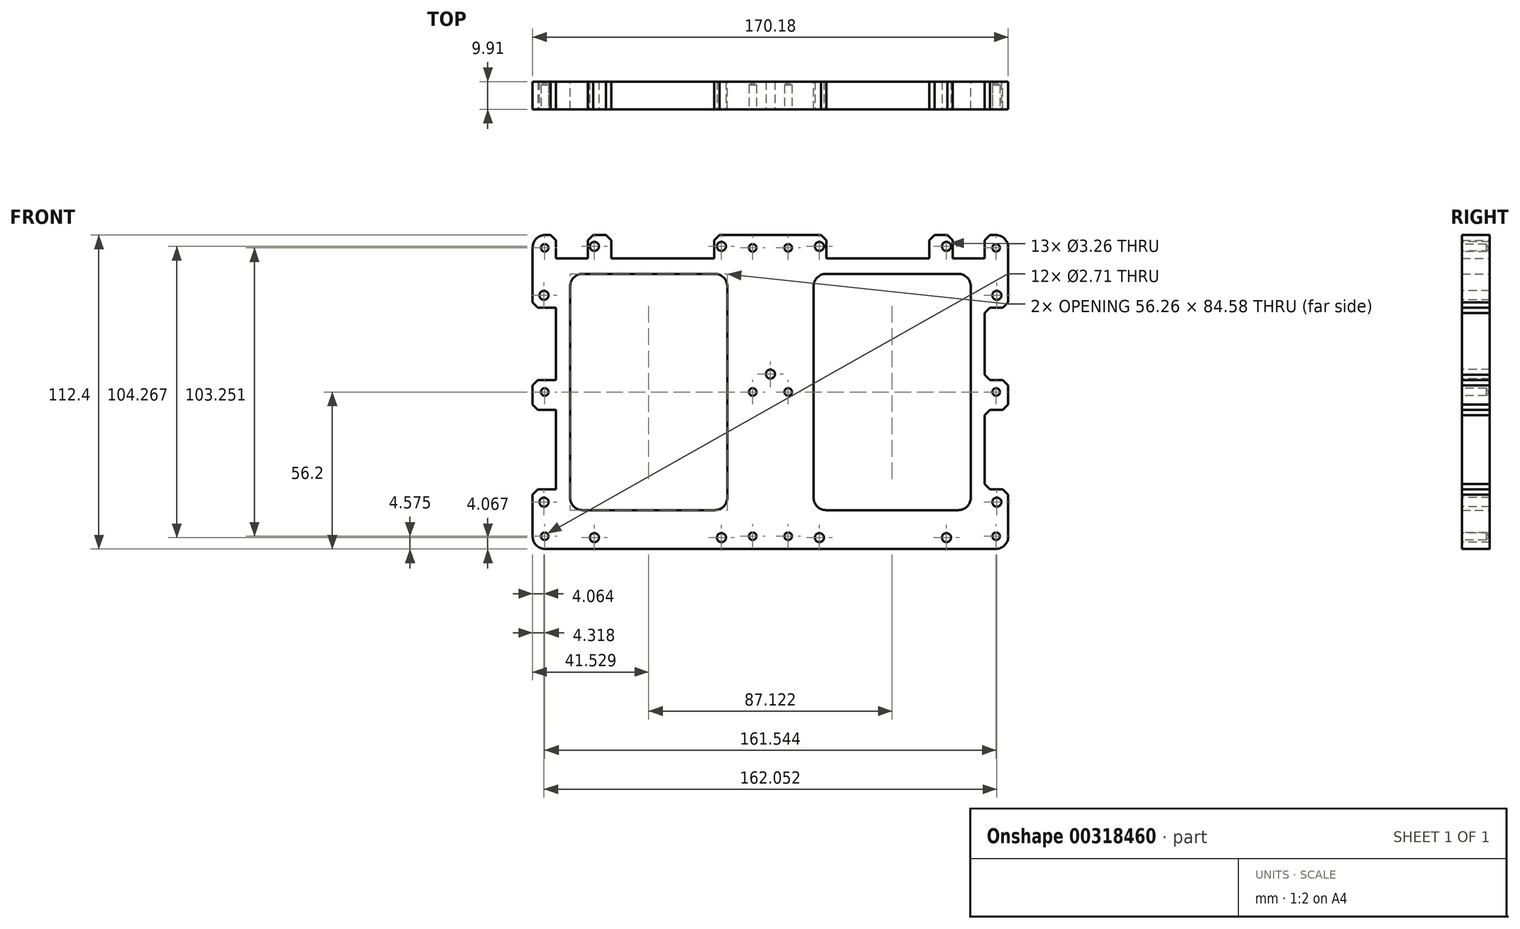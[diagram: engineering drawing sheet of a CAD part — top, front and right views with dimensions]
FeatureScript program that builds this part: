
annotation { "Feature Type Name" : "Feature", "Feature Type Description" : "" }
export const myFeature = defineFeature(function(context is Context, id is Id, definition is map)
    precondition{}
    {
        {
            var Q0;
            Q0=qCreatedBy(makeId("Front.planeOp"),FACE);
            var sketch = newSketch(context, id + "F0", { "sketchPlane" : qUnion([Q0])});
            skLineSegment(sketch, "E0.bottom", {"start": v(-80.64, -56.2) * mm, "end": v(80.64, -56.2) * mm});
            skLineSegment(sketch, "E0.top", {"start": v(-80.65, 56.2) * mm, "end": v(80.65, 56.2) * mm});
            skLineSegment(sketch, "E0.left", {"start": v(-85.09, -51.75) * mm, "end": v(-85.1, 51.75) * mm});
            skLineSegment(sketch, "E0.right", {"start": v(85.1, -56.2) * mm, "end": v(85.1, 56.2) * mm});
            skPoint(sketch, "E0.middle", {"position": v(0, 0) * mm});
            skLineSegment(sketch, "E1.bottom", {"start": v(-85.1, -34.86) * mm, "end": v(-76.7, -34.86) * mm});
            skLineSegment(sketch, "E1.top", {"start": v(-85.1, -6.41) * mm, "end": v(-76.7, -6.41) * mm});
            skLineSegment(sketch, "E1.left", {"start": v(-85.09, -34.86) * mm, "end": v(-85.09, -6.41) * mm});
            skLineSegment(sketch, "E1.right", {"start": v(-76.7, -34.86) * mm, "end": v(-76.7, -6.41) * mm});
            skLineSegment(sketch, "E2.bottom", {"start": v(-85.1, 4.25) * mm, "end": v(-76.7, 4.25) * mm});
            skLineSegment(sketch, "E2.top", {"start": v(-85.1, 30.16) * mm, "end": v(-76.7, 30.16) * mm});
            skLineSegment(sketch, "E2.left", {"start": v(-85.1, 4.25) * mm, "end": v(-85.1, 30.16) * mm});
            skLineSegment(sketch, "E2.right", {"start": v(-76.7, 4.25) * mm, "end": v(-76.7, 30.16) * mm});
            skLineSegment(sketch, "E3.bottom", {"start": v(-76.7, 56.2) * mm, "end": v(-65.28, 56.2) * mm});
            skLineSegment(sketch, "E3.top", {"start": v(-76.7, 47.82) * mm, "end": v(-65.28, 47.82) * mm});
            skLineSegment(sketch, "E3.left", {"start": v(-76.7, 56.2) * mm, "end": v(-76.7, 47.82) * mm});
            skLineSegment(sketch, "E3.right", {"start": v(-65.28, 56.2) * mm, "end": v(-65.28, 47.82) * mm});
            skPoint(sketch, "E4.oppositeSnap0", {"position": v(-71, 47.82) * mm});
            skLineSegment(sketch, "E4.bottom", {"start": v(-56.9, 56.2) * mm, "end": v(-20.07, 56.2) * mm});
            skLineSegment(sketch, "E4.top", {"start": v(-56.9, 47.82) * mm, "end": v(-20.07, 47.82) * mm});
            skLineSegment(sketch, "E4.left", {"start": v(-56.9, 56.2) * mm, "end": v(-56.9, 47.82) * mm});
            skLineSegment(sketch, "E4.right", {"start": v(-20.07, 56.2) * mm, "end": v(-20.07, 47.82) * mm});
            skLineSegment(sketch, "E5.bottom", {"start": v(-19.88, -42.3) * mm, "end": v(-67.25, -42.3) * mm});
            skLineSegment(sketch, "E5.top", {"start": v(-19.88, 42.3) * mm, "end": v(-67.25, 42.3) * mm});
            skLineSegment(sketch, "E5.left", {"start": v(-15.43, -37.85) * mm, "end": v(-15.43, 37.85) * mm});
            skLineSegment(sketch, "E5.right", {"start": v(-71.7, -37.85) * mm, "end": v(-71.7, 37.85) * mm});
            skPoint(sketch, "E5.middle", {"position": v(-43.56, 0) * mm});
            skPoint(sketch, "E6.visualSharp", {"position": v(-71.7, 42.3) * mm});
            skArc(sketch, "E6.filletArc", {"start": v(-67.25, 42.3) * mm, "mid": v(-70.39, 40.99) * mm, "end": v(-71.7, 37.85) * mm});
            skPoint(sketch, "E7.visualSharp", {"position": v(-15.43, 42.3) * mm});
            skArc(sketch, "E7.filletArc", {"start": v(-15.43, 37.85) * mm, "mid": v(-16.73, 40.99) * mm, "end": v(-19.88, 42.3) * mm});
            skPoint(sketch, "E8.visualSharp", {"position": v(-15.43, -42.3) * mm});
            skArc(sketch, "E8.filletArc", {"start": v(-19.88, -42.3) * mm, "mid": v(-16.73, -40.99) * mm, "end": v(-15.43, -37.85) * mm});
            skPoint(sketch, "E9.visualSharp", {"position": v(-71.7, -42.3) * mm});
            skArc(sketch, "E9.filletArc", {"start": v(-71.7, -37.85) * mm, "mid": v(-70.39, -40.99) * mm, "end": v(-67.25, -42.3) * mm});
            skArc(sketch, "E10.MirrorCS", {"start": v(71.7, -37.85) * mm, "mid": v(70.39, -40.99) * mm, "end": v(67.25, -42.3) * mm});
            skArc(sketch, "E11.MirrorCS", {"start": v(67.25, 42.3) * mm, "mid": v(70.39, 40.99) * mm, "end": v(71.7, 37.85) * mm});
            skLineSegment(sketch, "E12.MirrorCS", {"start": v(76.7, 47.82) * mm, "end": v(65.28, 47.82) * mm});
            skArc(sketch, "E13.MirrorCS", {"start": v(19.88, -42.3) * mm, "mid": v(16.73, -40.99) * mm, "end": v(15.43, -37.85) * mm});
            skArc(sketch, "E14.MirrorCS", {"start": v(15.43, 37.85) * mm, "mid": v(16.73, 40.99) * mm, "end": v(19.88, 42.3) * mm});
            skLineSegment(sketch, "E15.MirrorCS", {"start": v(65.28, 56.2) * mm, "end": v(65.28, 47.82) * mm});
            skLineSegment(sketch, "E16.MirrorCS", {"start": v(85.1, -6.41) * mm, "end": v(76.7, -6.41) * mm});
            skLineSegment(sketch, "E17.MirrorCS", {"start": v(56.9, 47.82) * mm, "end": v(20.07, 47.82) * mm});
            skPoint(sketch, "E18.MirrorP", {"position": v(71.7, 42.3) * mm});
            skLineSegment(sketch, "E19.MirrorCS", {"start": v(20.07, 56.2) * mm, "end": v(20.07, 47.82) * mm});
            skLineSegment(sketch, "E20.MirrorCS", {"start": v(56.9, 56.2) * mm, "end": v(20.07, 56.2) * mm});
            skLineSegment(sketch, "E21.MirrorCS", {"start": v(19.88, -42.3) * mm, "end": v(67.25, -42.3) * mm});
            skLineSegment(sketch, "E22.MirrorCS", {"start": v(71.7, -37.85) * mm, "end": v(71.7, 37.85) * mm});
            skPoint(sketch, "E23.MirrorP", {"position": v(71.7, -42.3) * mm});
            skLineSegment(sketch, "E24.MirrorCS", {"start": v(76.7, 56.2) * mm, "end": v(65.28, 56.2) * mm});
            skLineSegment(sketch, "E25.MirrorCS", {"start": v(76.7, 4.25) * mm, "end": v(76.7, 30.16) * mm});
            skLineSegment(sketch, "E26.MirrorCS", {"start": v(85.1, 4.25) * mm, "end": v(85.1, 30.16) * mm});
            skLineSegment(sketch, "E27.MirrorCS", {"start": v(85.1, 30.16) * mm, "end": v(76.7, 30.16) * mm});
            skLineSegment(sketch, "E28.MirrorCS", {"start": v(85.1, 4.25) * mm, "end": v(76.7, 4.25) * mm});
            skLineSegment(sketch, "E29.MirrorCS", {"start": v(76.7, -34.86) * mm, "end": v(76.7, -6.41) * mm});
            skLineSegment(sketch, "E30.MirrorCS", {"start": v(85.09, -34.86) * mm, "end": v(85.09, -6.41) * mm});
            skPoint(sketch, "E31.MirrorP", {"position": v(15.43, -42.3) * mm});
            skLineSegment(sketch, "E32.MirrorCS", {"start": v(85.1, -34.86) * mm, "end": v(76.7, -34.86) * mm});
            skLineSegment(sketch, "E33.MirrorCS", {"start": v(85.09, -51.75) * mm, "end": v(85.1, 51.75) * mm});
            skLineSegment(sketch, "E34.MirrorCS", {"start": v(76.7, 56.2) * mm, "end": v(76.7, 47.82) * mm});
            skLineSegment(sketch, "E35.MirrorCS", {"start": v(19.88, 42.3) * mm, "end": v(67.25, 42.3) * mm});
            skLineSegment(sketch, "E36.MirrorCS", {"start": v(15.43, -37.85) * mm, "end": v(15.43, 37.85) * mm});
            skPoint(sketch, "E37.MirrorP", {"position": v(71, 47.82) * mm});
            skLineSegment(sketch, "E38.MirrorCS", {"start": v(56.9, 56.2) * mm, "end": v(56.9, 47.82) * mm});
            skPoint(sketch, "E39.MirrorP", {"position": v(15.43, 42.3) * mm});
            skPoint(sketch, "E40.MirrorP", {"position": v(43.56, 0) * mm});
            skPoint(sketch, "E41.visualSharp", {"position": v(-85.1, 56.2) * mm});
            skArc(sketch, "E41.filletArc", {"start": v(-80.65, 56.2) * mm, "mid": v(-83.79, 54.9) * mm, "end": v(-85.1, 51.75) * mm});
            skPoint(sketch, "E42.visualSharp", {"position": v(-85.09, -56.2) * mm});
            skArc(sketch, "E42.filletArc", {"start": v(-85.09, -51.75) * mm, "mid": v(-83.79, -54.9) * mm, "end": v(-80.64, -56.2) * mm});
            skPoint(sketch, "E43.visualSharp", {"position": v(85.1, -56.2) * mm});
            skArc(sketch, "E43.filletArc", {"start": v(80.64, -56.2) * mm, "mid": v(83.79, -54.9) * mm, "end": v(85.09, -51.75) * mm});
            skPoint(sketch, "E44.visualSharp", {"position": v(85.09, 56.2) * mm});
            skArc(sketch, "E44.filletArc", {"start": v(85.1, 51.75) * mm, "mid": v(83.79, 54.9) * mm, "end": v(80.65, 56.2) * mm});
            skSolve(sketch);
        }
        {
            var Q0;
            {var subQ12=sQuery(id+"F0.wireOp",EDGE,"E0.bottom");Q0=makeQuery(id+"F0.imprint","IMPRINT",FACE,{"disambiguationData":[TD([[makeQuery(id+"F0.imprint","IMPRINT",EDGE,{"derivedFrom":subQ12}),1.0]])]});}
            extrude(context, id + "F1", {"entities" : qUnion([Q0]), "depth" : 9.9 * mm});
        }
        {
            var Q0;
            Q0=makeQuery(id+"F1.opExtrude","SWEPT_EDGE",EDGE,{"disambiguationData":[OSD([sQuery(id+"F0.wireOp",EDGE,"E0.left"),sQuery(id+"F0.wireOp",EDGE,"E1.bottom"),sQuery(id+"F0.wireOp",EDGE,"E1.left")])]});
            var Q1;
            Q1=makeQuery(id+"F1.opExtrude","SWEPT_EDGE",EDGE,{"disambiguationData":[OSD([sQuery(id+"F0.wireOp",EDGE,"E0.left"),sQuery(id+"F0.wireOp",EDGE,"E1.top"),sQuery(id+"F0.wireOp",EDGE,"E1.left")])]});
            var Q2;
            Q2=makeQuery(id+"F1.opExtrude","SWEPT_EDGE",EDGE,{"disambiguationData":[OSD([sQuery(id+"F0.wireOp",EDGE,"E0.left"),sQuery(id+"F0.wireOp",EDGE,"E2.bottom"),sQuery(id+"F0.wireOp",EDGE,"E2.left")])]});
            var Q3;
            Q3=makeQuery(id+"F1.opExtrude","SWEPT_EDGE",EDGE,{"disambiguationData":[OSD([sQuery(id+"F0.wireOp",EDGE,"E0.left"),sQuery(id+"F0.wireOp",EDGE,"E2.top"),sQuery(id+"F0.wireOp",EDGE,"E2.left")])]});
            var Q4;
            Q4=makeQuery(id+"F1.opExtrude","SWEPT_EDGE",EDGE,{"disambiguationData":[OSD([sQuery(id+"F0.wireOp",EDGE,"E0.top"),sQuery(id+"F0.wireOp",EDGE,"E3.bottom"),sQuery(id+"F0.wireOp",EDGE,"E3.left")])]});
            var Q5;
            Q5=makeQuery(id+"F1.opExtrude","SWEPT_EDGE",EDGE,{"disambiguationData":[OSD([sQuery(id+"F0.wireOp",EDGE,"E0.top"),sQuery(id+"F0.wireOp",EDGE,"E3.bottom"),sQuery(id+"F0.wireOp",EDGE,"E3.right")])]});
            var Q6;
            Q6=makeQuery(id+"F1.opExtrude","SWEPT_EDGE",EDGE,{"disambiguationData":[OSD([sQuery(id+"F0.wireOp",EDGE,"E0.top"),sQuery(id+"F0.wireOp",EDGE,"E4.bottom"),sQuery(id+"F0.wireOp",EDGE,"E4.left")])]});
            var Q7;
            Q7=makeQuery(id+"F1.opExtrude","SWEPT_EDGE",EDGE,{"disambiguationData":[OSD([sQuery(id+"F0.wireOp",EDGE,"E0.top"),sQuery(id+"F0.wireOp",EDGE,"E4.bottom"),sQuery(id+"F0.wireOp",EDGE,"E4.right")])]});
            var Q8;
            Q8=makeQuery(id+"F1.opExtrude","SWEPT_EDGE",EDGE,{"disambiguationData":[OSD([sQuery(id+"F0.wireOp",EDGE,"E0.top"),sQuery(id+"F0.wireOp",EDGE,"E19.MirrorCS"),sQuery(id+"F0.wireOp",EDGE,"E20.MirrorCS")])]});
            var Q9;
            Q9=makeQuery(id+"F1.opExtrude","SWEPT_EDGE",EDGE,{"disambiguationData":[OSD([sQuery(id+"F0.wireOp",EDGE,"E0.top"),sQuery(id+"F0.wireOp",EDGE,"E15.MirrorCS"),sQuery(id+"F0.wireOp",EDGE,"E24.MirrorCS")])]});
            var Q10;
            Q10=makeQuery(id+"F1.opExtrude","SWEPT_EDGE",EDGE,{"disambiguationData":[OSD([sQuery(id+"F0.wireOp",EDGE,"E0.top"),sQuery(id+"F0.wireOp",EDGE,"E20.MirrorCS"),sQuery(id+"F0.wireOp",EDGE,"E38.MirrorCS")])]});
            var Q11;
            Q11=makeQuery(id+"F1.opExtrude","SWEPT_EDGE",EDGE,{"disambiguationData":[OSD([sQuery(id+"F0.wireOp",EDGE,"E0.top"),sQuery(id+"F0.wireOp",EDGE,"E24.MirrorCS"),sQuery(id+"F0.wireOp",EDGE,"E34.MirrorCS")])]});
            var Q12;
            Q12=makeQuery(id+"F1.opExtrude","SWEPT_EDGE",EDGE,{"disambiguationData":[OSD([sQuery(id+"F0.wireOp",EDGE,"E27.MirrorCS"),sQuery(id+"F0.wireOp",EDGE,"E33.MirrorCS")])]});
            var Q13;
            Q13=makeQuery(id+"F1.opExtrude","SWEPT_EDGE",EDGE,{"disambiguationData":[OSD([sQuery(id+"F0.wireOp",EDGE,"E28.MirrorCS"),sQuery(id+"F0.wireOp",EDGE,"E33.MirrorCS")])]});
            var Q14;
            Q14=makeQuery(id+"F1.opExtrude","SWEPT_EDGE",EDGE,{"disambiguationData":[OSD([sQuery(id+"F0.wireOp",EDGE,"E16.MirrorCS"),sQuery(id+"F0.wireOp",EDGE,"E33.MirrorCS")])]});
            var Q15;
            Q15=makeQuery(id+"F1.opExtrude","SWEPT_EDGE",EDGE,{"disambiguationData":[OSD([sQuery(id+"F0.wireOp",EDGE,"E32.MirrorCS"),sQuery(id+"F0.wireOp",EDGE,"E33.MirrorCS")])]});
            chamfer(context, id + "F2", {"entities" : qUnion([Q0, Q1, Q2, Q3, Q4, Q5, Q6, Q7, Q8, Q9, Q10, Q11, Q12, Q13, Q14, Q15]), "width" : 1.9 * mm, "tangentPropagation" : true});
        }
        {
            var Q0;
            Q0=makeQuery(id+"F1.opExtrude","CAP_FACE",FACE,{"disambiguationData":[OSD([sQuery(id+"F0.wireOp",EDGE,"E0.bottom"),sQuery(id+"F0.wireOp",EDGE,"E0.top"),sQuery(id+"F0.wireOp",EDGE,"E0.left"),sQuery(id+"F0.wireOp",EDGE,"E1.bottom"),sQuery(id+"F0.wireOp",EDGE,"E1.top"),sQuery(id+"F0.wireOp",EDGE,"E1.right"),sQuery(id+"F0.wireOp",EDGE,"E2.bottom"),sQuery(id+"F0.wireOp",EDGE,"E2.top"),sQuery(id+"F0.wireOp",EDGE,"E2.right"),sQuery(id+"F0.wireOp",EDGE,"E3.top"),sQuery(id+"F0.wireOp",EDGE,"E3.left"),sQuery(id+"F0.wireOp",EDGE,"E3.right"),sQuery(id+"F0.wireOp",EDGE,"E4.top"),sQuery(id+"F0.wireOp",EDGE,"E4.left"),sQuery(id+"F0.wireOp",EDGE,"E4.right"),sQuery(id+"F0.wireOp",EDGE,"E5.bottom"),sQuery(id+"F0.wireOp",EDGE,"E5.top"),sQuery(id+"F0.wireOp",EDGE,"E5.left"),sQuery(id+"F0.wireOp",EDGE,"E5.right"),sQuery(id+"F0.wireOp",EDGE,"E6.filletArc"),sQuery(id+"F0.wireOp",EDGE,"E7.filletArc"),sQuery(id+"F0.wireOp",EDGE,"E8.filletArc"),sQuery(id+"F0.wireOp",EDGE,"E9.filletArc"),sQuery(id+"F0.wireOp",EDGE,"E10.MirrorCS"),sQuery(id+"F0.wireOp",EDGE,"E11.MirrorCS"),sQuery(id+"F0.wireOp",EDGE,"E12.MirrorCS"),sQuery(id+"F0.wireOp",EDGE,"E13.MirrorCS"),sQuery(id+"F0.wireOp",EDGE,"E14.MirrorCS"),sQuery(id+"F0.wireOp",EDGE,"E15.MirrorCS"),sQuery(id+"F0.wireOp",EDGE,"E16.MirrorCS"),sQuery(id+"F0.wireOp",EDGE,"E17.MirrorCS"),sQuery(id+"F0.wireOp",EDGE,"E19.MirrorCS"),sQuery(id+"F0.wireOp",EDGE,"E21.MirrorCS"),sQuery(id+"F0.wireOp",EDGE,"E22.MirrorCS"),sQuery(id+"F0.wireOp",EDGE,"E25.MirrorCS"),sQuery(id+"F0.wireOp",EDGE,"E27.MirrorCS"),sQuery(id+"F0.wireOp",EDGE,"E28.MirrorCS"),sQuery(id+"F0.wireOp",EDGE,"E29.MirrorCS"),sQuery(id+"F0.wireOp",EDGE,"E32.MirrorCS"),sQuery(id+"F0.wireOp",EDGE,"E33.MirrorCS"),sQuery(id+"F0.wireOp",EDGE,"E34.MirrorCS"),sQuery(id+"F0.wireOp",EDGE,"E35.MirrorCS"),sQuery(id+"F0.wireOp",EDGE,"E36.MirrorCS"),sQuery(id+"F0.wireOp",EDGE,"E38.MirrorCS"),sQuery(id+"F0.wireOp",EDGE,"E41.filletArc"),sQuery(id+"F0.wireOp",EDGE,"E42.filletArc"),sQuery(id+"F0.wireOp",EDGE,"E43.filletArc"),sQuery(id+"F0.wireOp",EDGE,"E44.filletArc")])],"isStart":false});
            var sketch = newSketch(context, id + "F3", { "sketchPlane" : qUnion([Q0])});
            skPoint(sketch, "E45", {"position": v(-80.77, 51.63) * mm});
            skPoint(sketch, "E46", {"position": v(-80.77, 0) * mm});
            skPoint(sketch, "E47", {"position": v(-80.77, -51.63) * mm});
            skPoint(sketch, "E48", {"position": v(-6.35, -51.63) * mm});
            skPoint(sketch, "E49", {"position": v(-6.35, 0) * mm});
            skPoint(sketch, "E50", {"position": v(-6.35, 51.63) * mm});
            skPoint(sketch, "E51.MirrorP", {"position": v(80.77, -51.63) * mm});
            skPoint(sketch, "E52.MirrorP", {"position": v(80.77, 51.63) * mm});
            skPoint(sketch, "E53.MirrorP", {"position": v(6.35, 51.63) * mm});
            skPoint(sketch, "E54.MirrorP", {"position": v(6.35, -51.63) * mm});
            skPoint(sketch, "E55.MirrorP", {"position": v(6.35, 0) * mm});
            skPoint(sketch, "E56.MirrorP", {"position": v(80.77, 0) * mm});
            skSolve(sketch);
        }
        {
            var Q0;
            Q0=sQuery(id+"F3.wireOp",VERTEX,"E45");
            var Q1;
            Q1=sQuery(id+"F3.wireOp",VERTEX,"E46");
            var Q2;
            Q2=sQuery(id+"F3.wireOp",VERTEX,"E47");
            var Q3;
            Q3=sQuery(id+"F3.wireOp",VERTEX,"E48");
            var Q4;
            Q4=sQuery(id+"F3.wireOp",VERTEX,"E49");
            var Q5;
            Q5=sQuery(id+"F3.wireOp",VERTEX,"E50");
            var Q6;
            Q6=sQuery(id+"F3.wireOp",VERTEX,"E53.MirrorP");
            var Q7;
            Q7=sQuery(id+"F3.wireOp",VERTEX,"E55.MirrorP");
            var Q8;
            Q8=sQuery(id+"F3.wireOp",VERTEX,"E54.MirrorP");
            var Q9;
            Q9=sQuery(id+"F3.wireOp",VERTEX,"E51.MirrorP");
            var Q10;
            Q10=sQuery(id+"F3.wireOp",VERTEX,"E56.MirrorP");
            var Q11;
            Q11=sQuery(id+"F3.wireOp",VERTEX,"E52.MirrorP");
            var Q12;
            Q12=makeQuery(id+"F1.opExtrude","SWEPT_BODY",BODY,{"disambiguationData":[OSD([sQuery(id+"F0.wireOp",EDGE,"E0.bottom"),sQuery(id+"F0.wireOp",EDGE,"E0.top"),sQuery(id+"F0.wireOp",EDGE,"E0.left"),sQuery(id+"F0.wireOp",EDGE,"E1.bottom"),sQuery(id+"F0.wireOp",EDGE,"E1.top"),sQuery(id+"F0.wireOp",EDGE,"E1.right"),sQuery(id+"F0.wireOp",EDGE,"E2.bottom"),sQuery(id+"F0.wireOp",EDGE,"E2.top"),sQuery(id+"F0.wireOp",EDGE,"E2.right"),sQuery(id+"F0.wireOp",EDGE,"E3.top"),sQuery(id+"F0.wireOp",EDGE,"E3.left"),sQuery(id+"F0.wireOp",EDGE,"E3.right"),sQuery(id+"F0.wireOp",EDGE,"E4.top"),sQuery(id+"F0.wireOp",EDGE,"E4.left"),sQuery(id+"F0.wireOp",EDGE,"E4.right"),sQuery(id+"F0.wireOp",EDGE,"E5.bottom"),sQuery(id+"F0.wireOp",EDGE,"E5.top"),sQuery(id+"F0.wireOp",EDGE,"E5.left"),sQuery(id+"F0.wireOp",EDGE,"E5.right"),sQuery(id+"F0.wireOp",EDGE,"E6.filletArc"),sQuery(id+"F0.wireOp",EDGE,"E7.filletArc"),sQuery(id+"F0.wireOp",EDGE,"E8.filletArc"),sQuery(id+"F0.wireOp",EDGE,"E9.filletArc"),sQuery(id+"F0.wireOp",EDGE,"E10.MirrorCS"),sQuery(id+"F0.wireOp",EDGE,"E11.MirrorCS"),sQuery(id+"F0.wireOp",EDGE,"E12.MirrorCS"),sQuery(id+"F0.wireOp",EDGE,"E13.MirrorCS"),sQuery(id+"F0.wireOp",EDGE,"E14.MirrorCS"),sQuery(id+"F0.wireOp",EDGE,"E15.MirrorCS"),sQuery(id+"F0.wireOp",EDGE,"E16.MirrorCS"),sQuery(id+"F0.wireOp",EDGE,"E17.MirrorCS"),sQuery(id+"F0.wireOp",EDGE,"E19.MirrorCS"),sQuery(id+"F0.wireOp",EDGE,"E21.MirrorCS"),sQuery(id+"F0.wireOp",EDGE,"E22.MirrorCS"),sQuery(id+"F0.wireOp",EDGE,"E25.MirrorCS"),sQuery(id+"F0.wireOp",EDGE,"E27.MirrorCS"),sQuery(id+"F0.wireOp",EDGE,"E28.MirrorCS"),sQuery(id+"F0.wireOp",EDGE,"E29.MirrorCS"),sQuery(id+"F0.wireOp",EDGE,"E32.MirrorCS"),sQuery(id+"F0.wireOp",EDGE,"E33.MirrorCS"),sQuery(id+"F0.wireOp",EDGE,"E34.MirrorCS"),sQuery(id+"F0.wireOp",EDGE,"E35.MirrorCS"),sQuery(id+"F0.wireOp",EDGE,"E36.MirrorCS"),sQuery(id+"F0.wireOp",EDGE,"E38.MirrorCS"),sQuery(id+"F0.wireOp",EDGE,"E41.filletArc"),sQuery(id+"F0.wireOp",EDGE,"E42.filletArc"),sQuery(id+"F0.wireOp",EDGE,"E43.filletArc"),sQuery(id+"F0.wireOp",EDGE,"E44.filletArc")])]});
            hole(context, id + "F4", {"style" : HoleStyle.SIMPLE, "endStyle" : HoleEndStyle.BLIND, "standardTappedOrClearance" : lookupTablePath({ "standard" : "ANSI", "engagement" : "75%", "pitch" : "32 tpi", "size" : "#6", "type" : "Tapped" }), "standardBlindInLast" : lookupTablePath({ "standard" : "ANSI", "engagement" : "75%", "pitch" : "32 tpi", "size" : "#6", "type" : "Tapped" }), "holeDiameter" : 2.7 * mm, "showTappedDepth" : true, "holeDepth" : 8.73 * mm, "tappedDepth" : 6.35 * mm, "tapClearance" : 3, "locations" : qUnion([Q0, Q1, Q2, Q3, Q4, Q5, Q6, Q7, Q8, Q9, Q10, Q11]), "scope" : qUnion([Q12]), "majorDiameter" : 3.5 * mm});
        }
        {
            var Q0;
            Q0=makeQuery(id+"F1.opExtrude","CAP_FACE",FACE,{"disambiguationData":[OSD([sQuery(id+"F0.wireOp",EDGE,"E0.bottom"),sQuery(id+"F0.wireOp",EDGE,"E0.top"),sQuery(id+"F0.wireOp",EDGE,"E0.left"),sQuery(id+"F0.wireOp",EDGE,"E1.bottom"),sQuery(id+"F0.wireOp",EDGE,"E1.top"),sQuery(id+"F0.wireOp",EDGE,"E1.right"),sQuery(id+"F0.wireOp",EDGE,"E2.bottom"),sQuery(id+"F0.wireOp",EDGE,"E2.top"),sQuery(id+"F0.wireOp",EDGE,"E2.right"),sQuery(id+"F0.wireOp",EDGE,"E3.top"),sQuery(id+"F0.wireOp",EDGE,"E3.left"),sQuery(id+"F0.wireOp",EDGE,"E3.right"),sQuery(id+"F0.wireOp",EDGE,"E4.top"),sQuery(id+"F0.wireOp",EDGE,"E4.left"),sQuery(id+"F0.wireOp",EDGE,"E4.right"),sQuery(id+"F0.wireOp",EDGE,"E5.bottom"),sQuery(id+"F0.wireOp",EDGE,"E5.top"),sQuery(id+"F0.wireOp",EDGE,"E5.left"),sQuery(id+"F0.wireOp",EDGE,"E5.right"),sQuery(id+"F0.wireOp",EDGE,"E6.filletArc"),sQuery(id+"F0.wireOp",EDGE,"E7.filletArc"),sQuery(id+"F0.wireOp",EDGE,"E8.filletArc"),sQuery(id+"F0.wireOp",EDGE,"E9.filletArc"),sQuery(id+"F0.wireOp",EDGE,"E10.MirrorCS"),sQuery(id+"F0.wireOp",EDGE,"E11.MirrorCS"),sQuery(id+"F0.wireOp",EDGE,"E12.MirrorCS"),sQuery(id+"F0.wireOp",EDGE,"E13.MirrorCS"),sQuery(id+"F0.wireOp",EDGE,"E14.MirrorCS"),sQuery(id+"F0.wireOp",EDGE,"E15.MirrorCS"),sQuery(id+"F0.wireOp",EDGE,"E16.MirrorCS"),sQuery(id+"F0.wireOp",EDGE,"E17.MirrorCS"),sQuery(id+"F0.wireOp",EDGE,"E19.MirrorCS"),sQuery(id+"F0.wireOp",EDGE,"E21.MirrorCS"),sQuery(id+"F0.wireOp",EDGE,"E22.MirrorCS"),sQuery(id+"F0.wireOp",EDGE,"E25.MirrorCS"),sQuery(id+"F0.wireOp",EDGE,"E27.MirrorCS"),sQuery(id+"F0.wireOp",EDGE,"E28.MirrorCS"),sQuery(id+"F0.wireOp",EDGE,"E29.MirrorCS"),sQuery(id+"F0.wireOp",EDGE,"E32.MirrorCS"),sQuery(id+"F0.wireOp",EDGE,"E33.MirrorCS"),sQuery(id+"F0.wireOp",EDGE,"E34.MirrorCS"),sQuery(id+"F0.wireOp",EDGE,"E35.MirrorCS"),sQuery(id+"F0.wireOp",EDGE,"E36.MirrorCS"),sQuery(id+"F0.wireOp",EDGE,"E38.MirrorCS"),sQuery(id+"F0.wireOp",EDGE,"E41.filletArc"),sQuery(id+"F0.wireOp",EDGE,"E42.filletArc"),sQuery(id+"F0.wireOp",EDGE,"E43.filletArc"),sQuery(id+"F0.wireOp",EDGE,"E44.filletArc")])],"isStart":false});
            var sketch = newSketch(context, id + "F5", { "sketchPlane" : qUnion([Q0])});
            skPoint(sketch, "E57", {"position": v(0, 6.41) * mm});
            skPoint(sketch, "E58", {"position": v(-17.53, 52.13) * mm});
            skPoint(sketch, "E59", {"position": v(-63, 52.13) * mm});
            skPoint(sketch, "E60", {"position": v(-81.03, 34.6) * mm});
            skPoint(sketch, "E61", {"position": v(-81.03, -39.43) * mm});
            skPoint(sketch, "E62", {"position": v(-63, -52.13) * mm});
            skPoint(sketch, "E63", {"position": v(-17.53, -52.13) * mm});
            skPoint(sketch, "E64.MirrorP", {"position": v(17.53, 52.13) * mm});
            skPoint(sketch, "E65.MirrorP", {"position": v(81.03, -39.43) * mm});
            skPoint(sketch, "E66.MirrorP", {"position": v(81.03, 34.6) * mm});
            skPoint(sketch, "E67.MirrorP", {"position": v(17.53, -52.13) * mm});
            skPoint(sketch, "E68.MirrorP", {"position": v(63, -52.13) * mm});
            skPoint(sketch, "E69.MirrorP", {"position": v(63, 52.13) * mm});
            skSolve(sketch);
        }
        {
            var Q0;
            Q0=sQuery(id+"F5.wireOp",VERTEX,"E60");
            var Q1;
            Q1=sQuery(id+"F5.wireOp",VERTEX,"E59");
            var Q2;
            Q2=sQuery(id+"F5.wireOp",VERTEX,"E61");
            var Q3;
            Q3=sQuery(id+"F5.wireOp",VERTEX,"E62");
            var Q4;
            Q4=sQuery(id+"F5.wireOp",VERTEX,"E58");
            var Q5;
            Q5=sQuery(id+"F5.wireOp",VERTEX,"E63");
            var Q6;
            Q6=sQuery(id+"F5.wireOp",VERTEX,"E57");
            var Q7;
            Q7=sQuery(id+"F5.wireOp",VERTEX,"E67.MirrorP");
            var Q8;
            Q8=sQuery(id+"F5.wireOp",VERTEX,"E68.MirrorP");
            var Q9;
            Q9=sQuery(id+"F5.wireOp",VERTEX,"E65.MirrorP");
            var Q10;
            Q10=sQuery(id+"F5.wireOp",VERTEX,"E66.MirrorP");
            var Q11;
            Q11=sQuery(id+"F5.wireOp",VERTEX,"E69.MirrorP");
            var Q12;
            Q12=sQuery(id+"F5.wireOp",VERTEX,"E64.MirrorP");
            var Q13;
            Q13=makeQuery(id+"F1.opExtrude","SWEPT_BODY",BODY,{"disambiguationData":[OSD([sQuery(id+"F0.wireOp",EDGE,"E0.bottom"),sQuery(id+"F0.wireOp",EDGE,"E0.top"),sQuery(id+"F0.wireOp",EDGE,"E0.left"),sQuery(id+"F0.wireOp",EDGE,"E1.bottom"),sQuery(id+"F0.wireOp",EDGE,"E1.top"),sQuery(id+"F0.wireOp",EDGE,"E1.right"),sQuery(id+"F0.wireOp",EDGE,"E2.bottom"),sQuery(id+"F0.wireOp",EDGE,"E2.top"),sQuery(id+"F0.wireOp",EDGE,"E2.right"),sQuery(id+"F0.wireOp",EDGE,"E3.top"),sQuery(id+"F0.wireOp",EDGE,"E3.left"),sQuery(id+"F0.wireOp",EDGE,"E3.right"),sQuery(id+"F0.wireOp",EDGE,"E4.top"),sQuery(id+"F0.wireOp",EDGE,"E4.left"),sQuery(id+"F0.wireOp",EDGE,"E4.right"),sQuery(id+"F0.wireOp",EDGE,"E5.bottom"),sQuery(id+"F0.wireOp",EDGE,"E5.top"),sQuery(id+"F0.wireOp",EDGE,"E5.left"),sQuery(id+"F0.wireOp",EDGE,"E5.right"),sQuery(id+"F0.wireOp",EDGE,"E6.filletArc"),sQuery(id+"F0.wireOp",EDGE,"E7.filletArc"),sQuery(id+"F0.wireOp",EDGE,"E8.filletArc"),sQuery(id+"F0.wireOp",EDGE,"E9.filletArc"),sQuery(id+"F0.wireOp",EDGE,"E10.MirrorCS"),sQuery(id+"F0.wireOp",EDGE,"E11.MirrorCS"),sQuery(id+"F0.wireOp",EDGE,"E12.MirrorCS"),sQuery(id+"F0.wireOp",EDGE,"E13.MirrorCS"),sQuery(id+"F0.wireOp",EDGE,"E14.MirrorCS"),sQuery(id+"F0.wireOp",EDGE,"E15.MirrorCS"),sQuery(id+"F0.wireOp",EDGE,"E16.MirrorCS"),sQuery(id+"F0.wireOp",EDGE,"E17.MirrorCS"),sQuery(id+"F0.wireOp",EDGE,"E19.MirrorCS"),sQuery(id+"F0.wireOp",EDGE,"E21.MirrorCS"),sQuery(id+"F0.wireOp",EDGE,"E22.MirrorCS"),sQuery(id+"F0.wireOp",EDGE,"E25.MirrorCS"),sQuery(id+"F0.wireOp",EDGE,"E27.MirrorCS"),sQuery(id+"F0.wireOp",EDGE,"E28.MirrorCS"),sQuery(id+"F0.wireOp",EDGE,"E29.MirrorCS"),sQuery(id+"F0.wireOp",EDGE,"E32.MirrorCS"),sQuery(id+"F0.wireOp",EDGE,"E33.MirrorCS"),sQuery(id+"F0.wireOp",EDGE,"E34.MirrorCS"),sQuery(id+"F0.wireOp",EDGE,"E35.MirrorCS"),sQuery(id+"F0.wireOp",EDGE,"E36.MirrorCS"),sQuery(id+"F0.wireOp",EDGE,"E38.MirrorCS"),sQuery(id+"F0.wireOp",EDGE,"E41.filletArc"),sQuery(id+"F0.wireOp",EDGE,"E42.filletArc"),sQuery(id+"F0.wireOp",EDGE,"E43.filletArc"),sQuery(id+"F0.wireOp",EDGE,"E44.filletArc")])]});
            hole(context, id + "F6", {"style" : HoleStyle.SIMPLE, "endStyle" : HoleEndStyle.THROUGH, "standardTappedOrClearance" : lookupTablePath({ "standard" : "ANSI", "fit" : "Normal (ASME)", "size" : "#4", "type" : "Clearance" }), "standardBlindInLast" : lookupTablePath({ "fit" : "Free", "standard" : "ANSI", "size" : "#4", "type" : "Clearance" }), "holeDiameter" : 3.26 * mm, "tappedDepth" : 6.36 * mm, "tapClearance" : 3, "locations" : qUnion([Q0, Q1, Q2, Q3, Q4, Q5, Q6, Q7, Q8, Q9, Q10, Q11, Q12]), "scope" : qUnion([Q13]), "majorDiameter" : 6.35 * mm});
        }
    });
